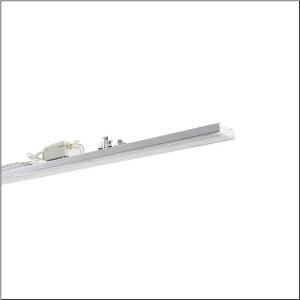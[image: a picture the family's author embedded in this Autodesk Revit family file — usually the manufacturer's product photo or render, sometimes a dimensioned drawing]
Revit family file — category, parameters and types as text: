
# Revit family: licross_21_recessed_mo_52te127n485g
name_source: partatom
category: Lighting Fixtures
units: mm (PartAtom-declared; Revit-internal decimal feet)

## family parameters
Cut with Voids When Loaded = No
Host = Face
Light Source = No
Part Type = Normal
Room Calculation Point = No
Round Connector Dimension = Use Diameter
Shared = No

## types (1)
- Licross 21 Recessed MO (1 x LED, 8820 lm, 47.9 W, 4000K)
    Apparent Load = 48 VA
    CIE Flux Codes = 72 92 99 100 100
    Color Rendering = 80
    Color Temperature = 4000K
    Default Elevation = 1800 mm
    Description = Licross 21 Recessed MO, luminaire insert, of sheet steel, galvanised, coil coated, white, length: 1.500mm, width: 66mm, height: 67mm, LED rated luminous flux: 8.820lm, light colour: 840, SDCM (Standard Deviation of Colour Matching)MacAdam ≤ 3 SDCM (initial), control gear: ON/OFF, with plug, 3-pole, with phase selection, mains connection: 220..240V, AC, 50/60Hz, rated input power: 48W, internal wiring halogen-free, primary optical cover: cover, of PMMA, light emission: direct distribution, primary light characteristic: symmetric, protection rating (complete): IP54, insulation class (complete): insulation class I (protective earthing), certification: CE, ENEC, VDE, UKCA, protection symbol: D if used in an environment with non-conductive dust loads with corresponding accessories, impact resistance: IK06, permissible ambient temperature for indoor applications: -35..+40°C, corresponds to IFS (International Featured Standards) requirements for safety and quality in the food industry, reducing of maximum allowable ambient temperature of 5°C with ceiling mounting, LABS conformity tested according to VDMA 24364:2018-05, The light source and the operating device comply with the requirements of the Ecodesign Regulation (EU) 2019/2020 and are replaceable in accordance with this regulation, packaging unit: 1 piece
    Height = 58 mm
    Lamp = 1 x LED
    Lamp Light Flux = 8820 lm
    Lamp Power = 47.9 W
    Lamp count = 1
    Length = 1500 mm
    Luminous efficacy = 184 lm/W
    Manufacturer = Siteco
    ModVariant = No
    Model = 52TE127N485G
    Mounting Place = Ceiling
    Mounting Type = Pendant
    Number of Poles = 1
    OnlyDefault = Yes
    Power Factor = 1
    Product Name = Licross 21 Recessed MO
    Product group = luminaire insert | ceiling pendant
    ProductGroupID = 901
    Protection Class = Protection class I
    Protection Degree = IP 54
    RLX_Detail_Level = 1
    RLX_Emergency_Light_Flux = 0 lm
    RLX_Emergency_Type = 0
    RLX_Emergency_Type_DB = No
    RlxData = <blob elided: 21213 chars, md5=0b4ddc1a>
    Socket = socket
    Standby Power = 0 W
    System Light Flux = 8820 lm
    System Power = 48 W
    Type Comments = Product without accessories
    Type Image = l_1296930.jpg
    URL = http://relux.com
    VarID = ---
    Voltage = 0 V
    Weight = 0.00 kg
    Width = 66 mm

## geometry (parser evidence)
native form markers: Blend x4, Sweep x10
no freeform markers — native parametric forms only
